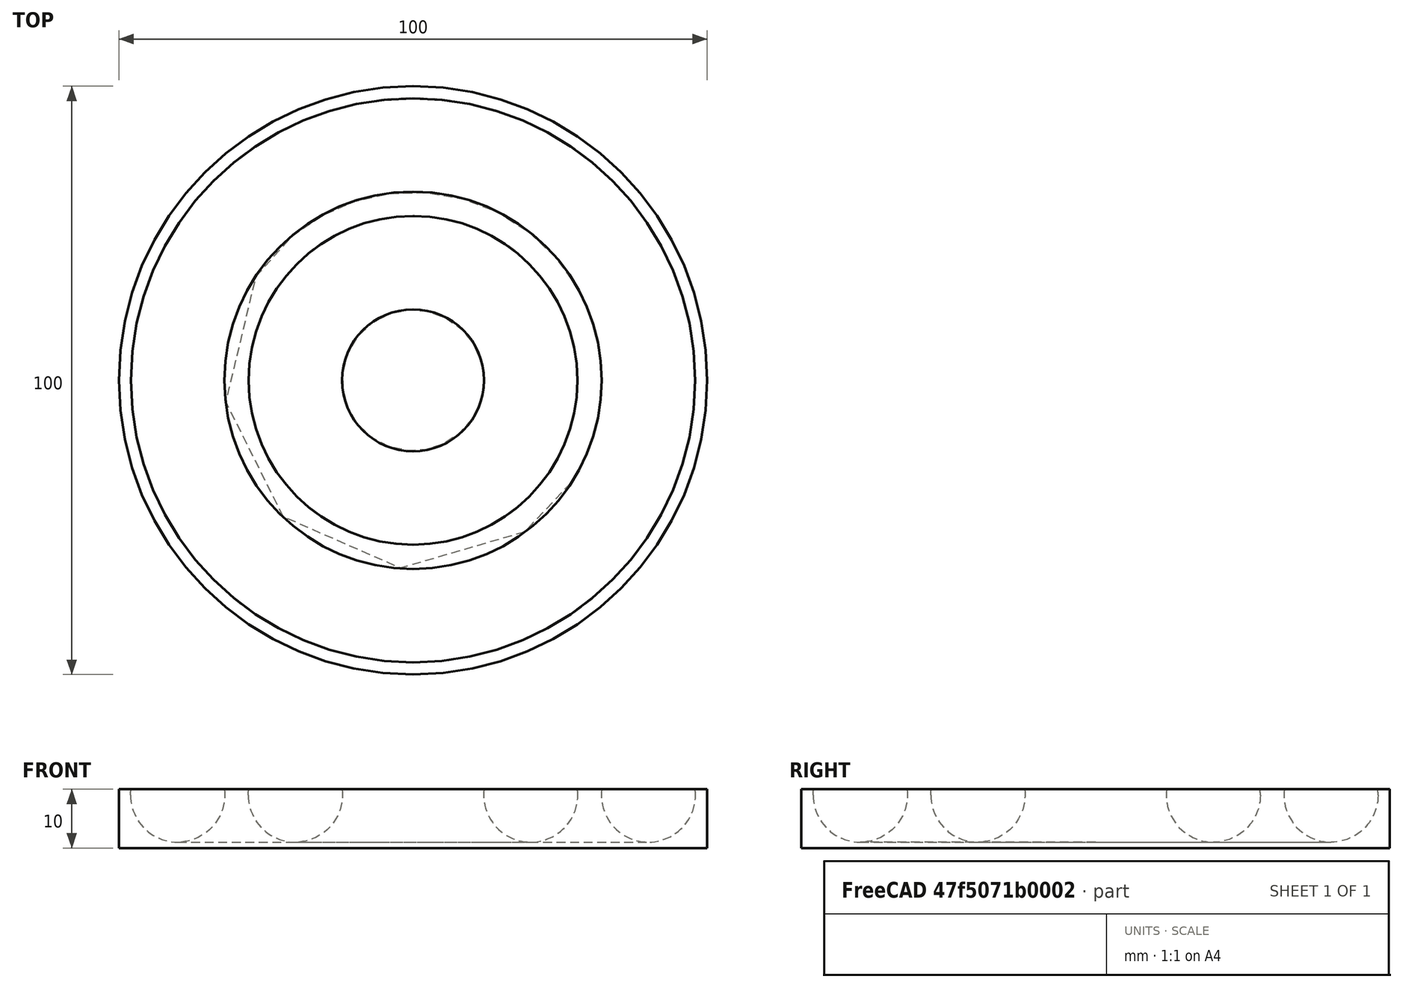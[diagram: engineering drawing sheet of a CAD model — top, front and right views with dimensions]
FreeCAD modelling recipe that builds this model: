
FCSTD DOCUMENT  (FreeCAD 0.16R6707 (Git))
Label: portacanicas
License: CreativeCommons Attribution-ShareAlike
LicenseURL: http://creativecommons.org/licenses/by-sa/4.0/
objects: Part::Torus×2, Part::Cylinder×1, Part::MultiFuse×1, Part::Cut×1
note: 5 computed .brp shape members not serialized (recipe doc carries the construction recipe); baked Part::Feature solids carry a one-line shape summary decoded from their .brp

FEATURE [Part::Cylinder] Cylinder  label="Base"
  Angle = 360
  Height = 10
  Radius = 50
FEATURE [Part::Torus] Torus  label="Canal_pequeña"
  Angle1 = -180
  Angle2 = 180
  Angle3 = 360
  Placement = pos=(0,0,9) rot=(0,0,1;0rad)
  Radius1 = 20
  Radius2 = 8
FEATURE [Part::Torus] Torus001  label="Canal_Grande"
  Angle1 = -180
  Angle2 = 180
  Angle3 = 360
  Placement = pos=(0,0,9) rot=(0,0,1;0rad)
  Radius1 = 40
  Radius2 = 8
FEATURE [Part::MultiFuse] Fusion  label="Canales"
  Shapes = -> [Torus001,Torus]
FEATURE [Part::Cut] Cut  label="Portacanicas"
  Base = -> Cylinder
  Tool = -> Fusion
